# Revit family: Flush_Valve-Urinal-American_Standard-Ultima_Sensor-6145SM_Series
name_source: partatom
category: Plumbing Fixtures
revit_build: Autodesk Revit 2014 (Build: 20130308_1515(x64)
units: mm (PartAtom-declared; Revit-internal decimal feet)

## types (3) — shared parameters
ADA Compliant = Yes
Assembly Code = D2020300
CW Connection = Yes
CWFU = 10
Cold Water Connection Diameter = 3/4"
Cold Water Connection Height = 11 1/2"
Cold Water Connection Radius = 3/8"
Default Elevation = 0"
Description = Ultima Sensor-Operated Urinal Flush Valve Diaphragm-Type
Finish = Brass-American Standard-002-Polished Chrome
HW Connection = No
Height = 14 5/8"
Installation Type = Surface Mounted
Manufacturer = American Standard
Material = Metal-American Standard-002-Polished Chrome
Price = Prices may vary. Please consult Manufacturer Representative for most up-to-date price list.
URL = http://www.americanstandard-us.com
Vent Connection = No
Warranty Information = 1 Year Limited Warranty
Waste Connection = No
zero-valued in all types: HWFU, WFU

## per-type parameters (varying)
| type | Flush Rate |
| 6145SM013.002 | 0.125 gpf (0.5 Lpf) |
| 6145SM051.002 | 0.5 gpf (0.9 Lpf) |
| 6145SM101.002 | 1.0 gpf (3.8 Lpf) |

note: column(s) folded — value = type name in every type: Model

## geometry (parser evidence)
native form markers: Sweep x2
no freeform markers — native parametric forms only
